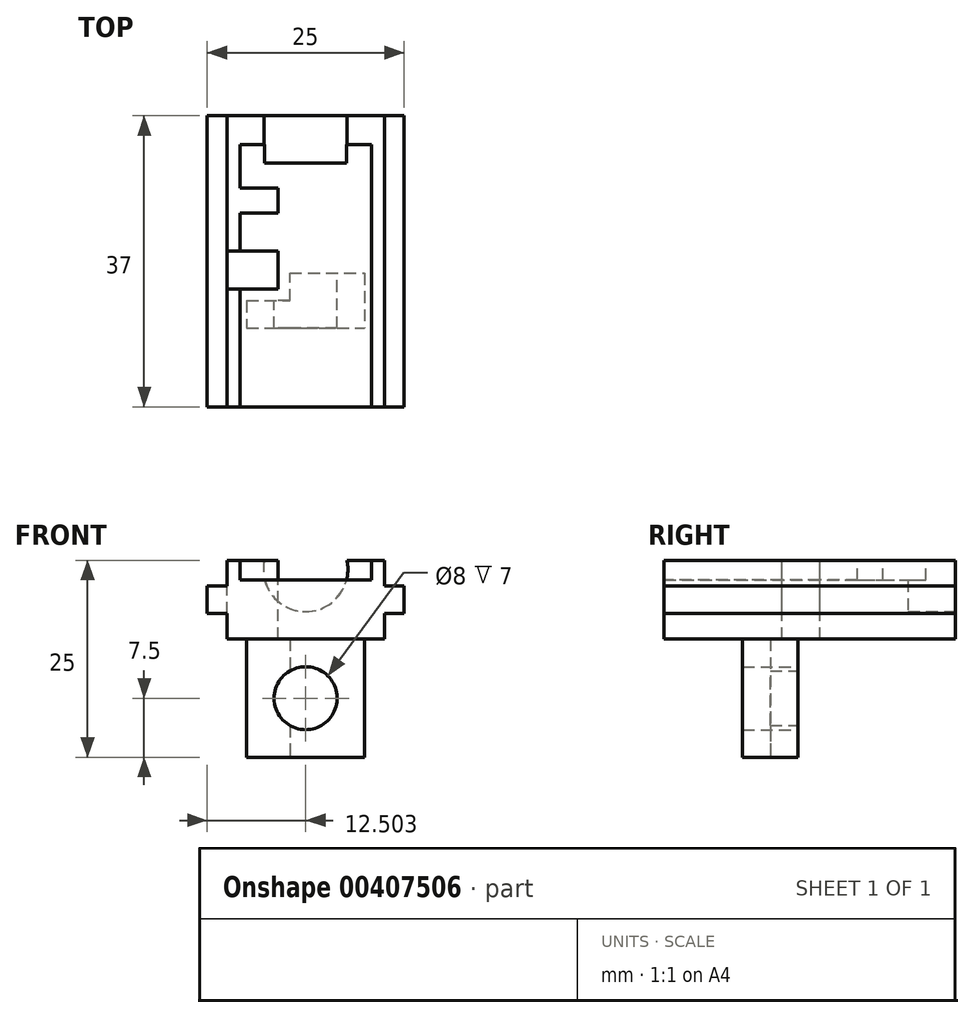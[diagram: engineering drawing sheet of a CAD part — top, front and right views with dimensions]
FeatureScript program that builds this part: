
annotation { "Feature Type Name" : "Feature", "Feature Type Description" : "" }
export const myFeature = defineFeature(function(context is Context, id is Id, definition is map)
    precondition{}
    {
        {
            var Q0;
            Q0=qCreatedBy(makeId("Top.planeOp"),FACE);
            var sketch = newSketch(context, id + "F0", { "sketchPlane" : qUnion([Q0])});
            skLineSegment(sketch, "E0.bottom", {"start": v(-20.4, 37) * mm, "end": v(-0.4, 37) * mm});
            skLineSegment(sketch, "E0.top", {"start": v(-20.4, 0) * mm, "end": v(-0.4, 0) * mm});
            skLineSegment(sketch, "E0.left", {"start": v(-20.4, 37) * mm, "end": v(-20.4, 0) * mm});
            skLineSegment(sketch, "E0.right", {"start": v(-0.4, 37) * mm, "end": v(-0.4, 0) * mm});
            skSolve(sketch);
        }
        {
            var Q0;
            Q0 = qSketchRegion(id + "F0", true);
            extrude(context, id + "F1", {"entities" : qUnion([Q0]), "depth" : 10 * mm});
        }
        {
            var Q0;
            Q0=makeQuery(id+"F1.opExtrude","SWEPT_FACE",FACE,{"disambiguationData":[OSD([sQuery(id+"F0.wireOp",EDGE,"E0.left")])]});
            var sketch = newSketch(context, id + "F2", { "sketchPlane" : qUnion([Q0])});
            skLineSegment(sketch, "E1.bottom", {"start": v(-37, 3.25) * mm, "end": v(0, 3.25) * mm});
            skLineSegment(sketch, "E1.top", {"start": v(-37, 6.75) * mm, "end": v(0, 6.75) * mm});
            skLineSegment(sketch, "E1.left", {"start": v(-37, 3.25) * mm, "end": v(-37, 6.75) * mm});
            skLineSegment(sketch, "E1.right", {"start": v(0, 3.25) * mm, "end": v(0, 6.75) * mm});
            skSolve(sketch);
        }
        {
            var Q0;
            Q0=makeQuery(id+"F1.opExtrude","SWEPT_FACE",FACE,{"disambiguationData":[OSD([sQuery(id+"F0.wireOp",EDGE,"E0.right")])]});
            var sketch = newSketch(context, id + "F3", { "sketchPlane" : qUnion([Q0])});
            skLineSegment(sketch, "E2.bottom", {"start": v(37, 6.75) * mm, "end": v(0, 6.75) * mm});
            skLineSegment(sketch, "E2.top", {"start": v(37, 3.25) * mm, "end": v(0, 3.25) * mm});
            skLineSegment(sketch, "E2.left", {"start": v(37, 6.75) * mm, "end": v(37, 3.25) * mm});
            skLineSegment(sketch, "E2.right", {"start": v(0, 6.75) * mm, "end": v(0, 3.25) * mm});
            skSolve(sketch);
        }
        {
            var Q0;
            Q0 = qSketchRegion(id + "F2", true);
            var Q1;
            Q1 = qSketchRegion(id + "F3", true);
            extrude(context, id + "F4", {"entities" : qUnion([Q0, Q1]), "operationType" : NewBodyOperationType.ADD, "depth" : 2.5 * mm, "hasSecondDirection" : true, "secondDirectionOppositeDirection" : true, "secondDirectionDepth" : 2.5 * mm});
        }
        {
            var Q0;
            Q0=makeQuery(id+"F1.opExtrude","CAP_FACE",FACE,{"disambiguationData":[OSD([sQuery(id+"F0.wireOp",EDGE,"E0.bottom"),sQuery(id+"F0.wireOp",EDGE,"E0.top"),sQuery(id+"F0.wireOp",EDGE,"E0.left"),sQuery(id+"F0.wireOp",EDGE,"E0.right")])],"isStart":false});
            var sketch = newSketch(context, id + "F5", { "sketchPlane" : qUnion([Q0])});
            skLineSegment(sketch, "E3.bottom", {"start": v(-18.75, 0) * mm, "end": v(-2.05, 0) * mm});
            skLineSegment(sketch, "E3.top", {"start": v(-18.75, 33.3) * mm, "end": v(-2.05, 33.3) * mm});
            skLineSegment(sketch, "E3.right", {"start": v(-2.05, 0) * mm, "end": v(-2.05, 33.3) * mm});
            skLineSegment(sketch, "E4", {"start": v(-18.75, 24.6) * mm, "end": v(-13.9, 24.6) * mm});
            skLineSegment(sketch, "E5", {"start": v(-13.9, 24.6) * mm, "end": v(-13.9, 27.8) * mm});
            skLineSegment(sketch, "E6", {"start": v(-13.9, 27.8) * mm, "end": v(-18.75, 27.8) * mm});
            skLineSegment(sketch, "E7", {"start": v(-18.75, 27.8) * mm, "end": v(-18.75, 33.3) * mm});
            skLineSegment(sketch, "E8", {"start": v(-18.75, 24.6) * mm, "end": v(-18.75, 19.8) * mm});
            skLineSegment(sketch, "E9", {"start": v(-18.75, 19.8) * mm, "end": v(-13.9, 19.8) * mm});
            skLineSegment(sketch, "E10", {"start": v(-13.9, 19.8) * mm, "end": v(-13.9, 15) * mm});
            skLineSegment(sketch, "E11", {"start": v(-13.9, 15) * mm, "end": v(-18.75, 15) * mm});
            skLineSegment(sketch, "E12", {"start": v(-18.75, 15) * mm, "end": v(-18.75, 0) * mm});
            skSolve(sketch);
        }
        {
            var Q0;
            Q0 = qSketchRegion(id + "F5", true);
            extrude(context, id + "F6", {"entities" : qUnion([Q0]), "operationType" : NewBodyOperationType.REMOVE, "oppositeDirection" : true, "depth" : 2.5 * mm});
        }
        {
            var Q0;
            Q0=makeQuery(id+"F1.opExtrude","CAP_FACE",FACE,{"disambiguationData":[OSD([sQuery(id+"F0.wireOp",EDGE,"E0.bottom"),sQuery(id+"F0.wireOp",EDGE,"E0.top"),sQuery(id+"F0.wireOp",EDGE,"E0.left"),sQuery(id+"F0.wireOp",EDGE,"E0.right")])],"isStart":false});
            var sketch = newSketch(context, id + "F7", { "sketchPlane" : qUnion([Q0])});
            skLineSegment(sketch, "E13", {"start": v(-18.75, 19.8) * mm, "end": v(-20.4, 19.8) * mm});
            skLineSegment(sketch, "E14", {"start": v(-20.4, 19.8) * mm, "end": v(-20.4, 15) * mm});
            skLineSegment(sketch, "E15", {"start": v(-20.4, 15) * mm, "end": v(-13.9, 15) * mm});
            skLineSegment(sketch, "E16", {"start": v(-13.9, 15) * mm, "end": v(-13.9, 19.8) * mm});
            skLineSegment(sketch, "E17", {"start": v(-13.9, 19.8) * mm, "end": v(-18.75, 19.8) * mm});
            skSolve(sketch);
        }
        {
            var Q0;
            Q0=makeQuery(id+"F1.opExtrude","CAP_FACE",FACE,{"disambiguationData":[OSD([sQuery(id+"F0.wireOp",EDGE,"E0.bottom"),sQuery(id+"F0.wireOp",EDGE,"E0.top"),sQuery(id+"F0.wireOp",EDGE,"E0.left"),sQuery(id+"F0.wireOp",EDGE,"E0.right")])],"isStart":true});
            var sketch = newSketch(context, id + "F8", { "sketchPlane" : qUnion([Q0])});
            skLineSegment(sketch, "E18.bottom", {"start": v(-17.9, -17) * mm, "end": v(-2.9, -17) * mm});
            skLineSegment(sketch, "E18.top", {"start": v(-17.9, -10) * mm, "end": v(-2.9, -10) * mm});
            skLineSegment(sketch, "E18.left", {"start": v(-17.9, -17) * mm, "end": v(-17.9, -10) * mm});
            skLineSegment(sketch, "E18.right", {"start": v(-2.9, -17) * mm, "end": v(-2.9, -10) * mm});
            skSolve(sketch);
        }
        {
            var Q0;
            Q0=makeQuery(id+"F8.imprint","IMPRINT",FACE,{"disambiguationData":[TD([[makeQuery(id+"F8.imprint","IMPRINT",EDGE,{"derivedFrom":sQuery(id+"F8.wireOp",EDGE,"E18.bottom")}),1.0]])]});
            extrude(context, id + "F9", {"entities" : qUnion([Q0]), "operationType" : NewBodyOperationType.ADD, "depth" : 15 * mm});
        }
        {
            var Q0;
            Q0=makeQuery(id+"F9.opExtrude","SWEPT_FACE",FACE,{"disambiguationData":[OSD([sQuery(id+"F8.wireOp",EDGE,"E18.bottom")])]});
            var sketch = newSketch(context, id + "F10", { "sketchPlane" : qUnion([Q0])});
            skCircle(sketch, "E19", {"center": v(10.4, -7.5) * mm, "radius": 4 * mm});
            skSolve(sketch);
        }
        {
            var Q0;
            Q0=makeQuery(id+"F10.imprint","IMPRINT",FACE,{"disambiguationData":[TD([[makeQuery(id+"F10.imprint","IMPRINT",EDGE,{"derivedFrom":sQuery(id+"F10.wireOp",EDGE,"E19")}),1.0]])]});
            extrude(context, id + "F11", {"entities" : qUnion([Q0]), "operationType" : NewBodyOperationType.REMOVE, "endBound" : BoundingType.THROUGH_ALL, "oppositeDirection" : true, "depth" : 40 * mm});
        }
        {
            var Q0;
            Q0=makeQuery(id+"F7.imprint","IMPRINT",FACE,{"disambiguationData":[TD([[makeQuery(id+"F7.imprint","IMPRINT",EDGE,{"derivedFrom":sQuery(id+"F7.wireOp",EDGE,"E13")}),1.0]])]});
            extrude(context, id + "F12", {"entities" : qUnion([Q0]), "operationType" : NewBodyOperationType.REMOVE, "endBound" : BoundingType.THROUGH_ALL, "oppositeDirection" : true, "depth" : 25 * mm});
        }
        {
            var Q0;
            Q0=makeQuery(id+"F9.opExtrude","CAP_FACE",FACE,{"disambiguationData":[OSD([sQuery(id+"F8.wireOp",EDGE,"E18.bottom"),sQuery(id+"F8.wireOp",EDGE,"E18.top"),sQuery(id+"F8.wireOp",EDGE,"E18.left"),sQuery(id+"F8.wireOp",EDGE,"E18.right")])],"isStart":false});
            var sketch = newSketch(context, id + "F13", { "sketchPlane" : qUnion([Q0])});
            skLineSegment(sketch, "E20", {"start": v(-17.9, -13.5) * mm, "end": v(-12.4, -13.5) * mm});
            skLineSegment(sketch, "E21", {"start": v(-12.4, -13.5) * mm, "end": v(-12.4, -17) * mm});
            skSolve(sketch);
        }
        {
            var Q0;
            {var subQ6=sQuery(id+"F13.wireOp",EDGE,"E20");Q0=makeQuery(id+"F13.imprint","IMPRINT",FACE,{"disambiguationData":[TD([[makeQuery(id+"F13.imprint","IMPRINT",EDGE,{"derivedFrom":subQ6}),-1.0]])]});}
            var Q1;
            Q1=makeQuery(id+"F1.opExtrude","CAP_FACE",FACE,{"disambiguationData":[OSD([sQuery(id+"F0.wireOp",EDGE,"E0.bottom"),sQuery(id+"F0.wireOp",EDGE,"E0.top"),sQuery(id+"F0.wireOp",EDGE,"E0.left"),sQuery(id+"F0.wireOp",EDGE,"E0.right")])],"isStart":true});
            extrude(context, id + "F14", {"entities" : qUnion([Q0]), "operationType" : NewBodyOperationType.REMOVE, "endBound" : BoundingType.UP_TO_SURFACE, "oppositeDirection" : true, "endBoundEntityFace" : qUnion([Q1]), "depth" : 25 * mm});
        }
        {
            var Q0;
            Q0=makeQuery(id+"F4.boolean.opBoolean","MERGE",FACE,{"derivedFrom":[makeQuery(id+"F1.opExtrude","SWEPT_FACE",FACE,{"disambiguationData":[OSD([sQuery(id+"F0.wireOp",EDGE,"E0.bottom")])]}),makeQuery(id+"F4.opExtrude","SWEPT_FACE",FACE,{"disambiguationData":[OSD([sQuery(id+"F2.wireOp",EDGE,"E1.left")])]}),makeQuery(id+"F4.opExtrude","SWEPT_FACE",FACE,{"disambiguationData":[OSD([sQuery(id+"F3.wireOp",EDGE,"E2.left")])]})]});
            var sketch = newSketch(context, id + "F15", { "sketchPlane" : qUnion([Q0])});
            skLineSegment(sketch, "E22", {"start": v(10.4, 10) * mm, "end": v(10.4, 3.5) * mm, "construction": true});
            skLineSegment(sketch, "E23", {"start": v(10.4, 10) * mm, "end": v(15.65, 10) * mm, "construction": true});
            skLineSegment(sketch, "E24", {"start": v(10.4, 10) * mm, "end": v(5.15, 10) * mm, "construction": true});
            skArc(sketch, "E25", {"start": v(5.15, 10) * mm, "mid": v(10.4, 3.5) * mm, "end": v(15.65, 10) * mm});
            skSolve(sketch);
        }
        {
            var Q0;
            {var subQ0=sQuery(id+"F15.wireOp",EDGE,"E25");Q0=makeQuery(id+"F15.imprint","IMPRINT",FACE,{"disambiguationData":[TD([[makeQuery(id+"F15.imprint","IMPRINT",EDGE,{"derivedFrom":subQ0}),1.0]])]});}
            extrude(context, id + "F16", {"entities" : qUnion([Q0]), "operationType" : NewBodyOperationType.REMOVE, "oppositeDirection" : true, "depth" : 6 * mm});
        }
    });
